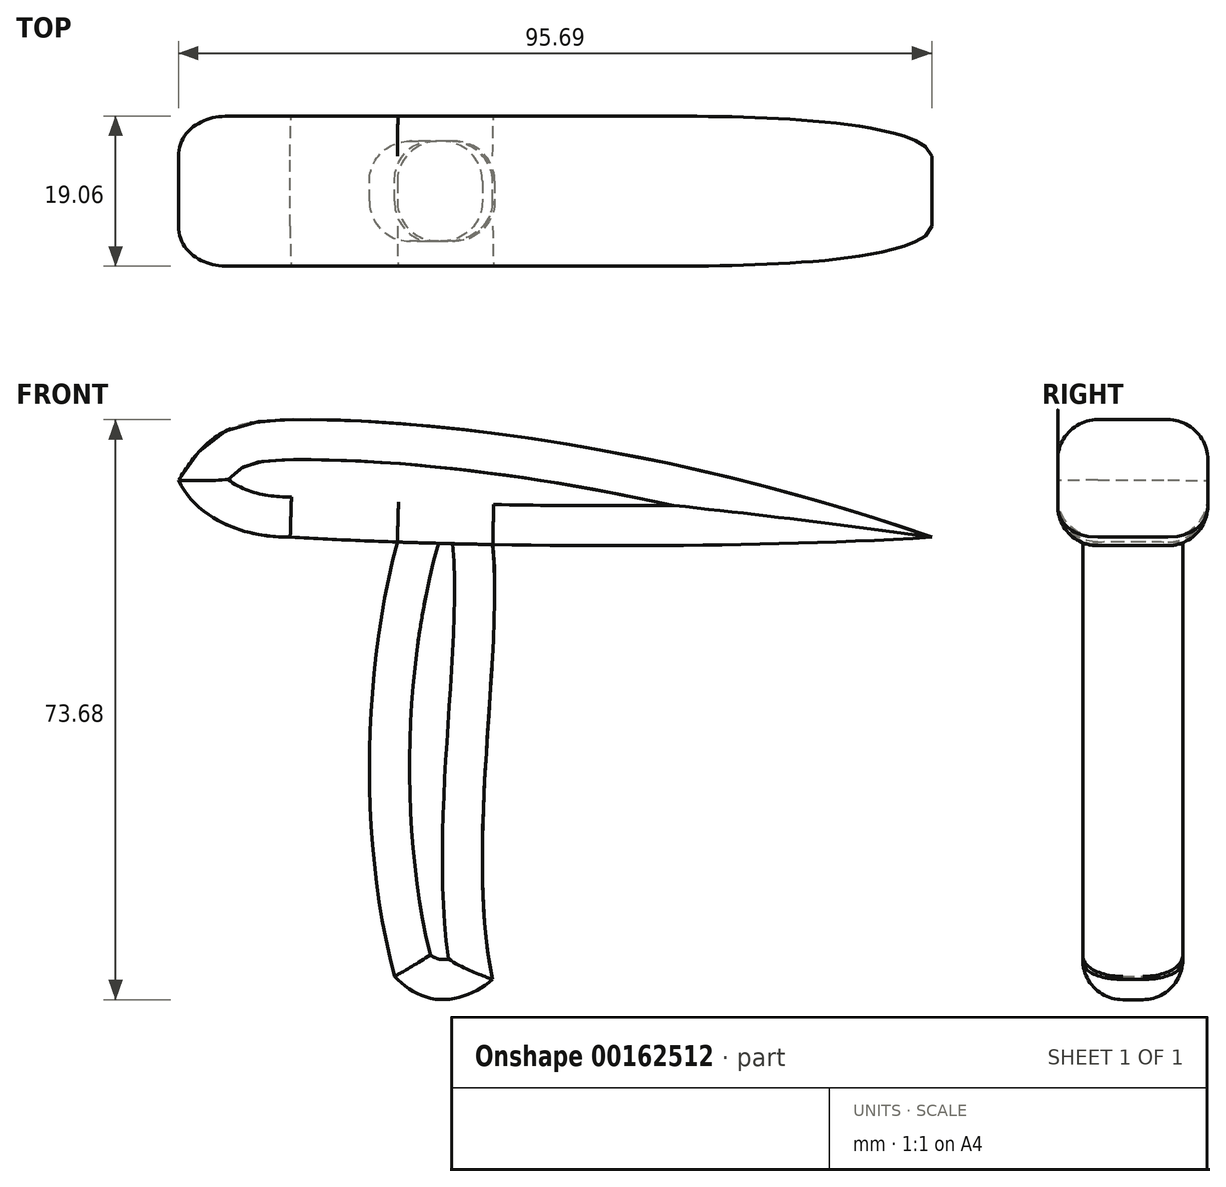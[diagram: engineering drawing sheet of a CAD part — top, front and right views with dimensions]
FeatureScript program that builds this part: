
annotation { "Feature Type Name" : "Feature", "Feature Type Description" : "" }
export const myFeature = defineFeature(function(context is Context, id is Id, definition is map)
    precondition{}
    {
        {
            var Q0;
            Q0=qCreatedBy(makeId("Front.planeOp"),FACE);
            var sketch = newSketch(context, id + "F0", { "sketchPlane" : qUnion([Q0])});
            skFitSpline(sketch, "E0", {"points": [v(-18.74, 0) * mm, v(-32.94, 7.24) * mm], "startDerivative": vector(-21.3, 0) * mm, "endDerivative": vector(-5.96, 12.78) * mm});
            skFitSpline(sketch, "E1", {"points": [v(-32.94, 7.24) * mm, v(-18.74, 14.9) * mm, v(62.75, 0) * mm], "startDerivative": vector(40.42, 66.4) * mm, "endDerivative": vector(151.04, -52.56) * mm});
            skFitSpline(sketch, "E2", {"points": [v(-18.74, 0) * mm, v(62.75, 0) * mm], "startDerivative": vector(64.51, -3.85) * mm, "endDerivative": vector(77.53, 4.86) * mm});
            skFitSpline(sketch, "E3", {"points": [v(-5.14, -0.63) * mm, v(-5.5, -55.81) * mm], "startDerivative": vector(-13.18, -49.42) * mm, "endDerivative": vector(13.65, -52) * mm});
            skFitSpline(sketch, "E4", {"points": [v(6.99, -0.94) * mm, v(6.97, -56.18) * mm], "startDerivative": vector(4.1, -40.3) * mm, "endDerivative": vector(10.6, -49.2) * mm});
            skFitSpline(sketch, "E5", {"points": [v(-5.5, -55.81) * mm, v(6.97, -56.18) * mm], "startDerivative": vector(11.23, -11.78) * mm, "endDerivative": vector(12.55, 10.29) * mm});
            skLineSegment(sketch, "E6", {"start": v(-5.14, -0.63) * mm, "end": v(6.99, -0.94) * mm});
            skSolve(sketch);
        }
        {
            var Q0;
            {var subQ3=sQuery(id+"F0.wireOp",EDGE,"E0");Q0=makeQuery(id+"F0.imprint","IMPRINT",FACE,{"disambiguationData":[TD([[makeQuery(id+"F0.imprint","IMPRINT",EDGE,{"derivedFrom":subQ3}),-1.0]])]});}
            var Q1;
            {var subQ1=sQuery(id+"F0.wireOp",EDGE,"E3");Q1=makeQuery(id+"F0.imprint","IMPRINT",FACE,{"disambiguationData":[TD([[makeQuery(id+"F0.imprint","IMPRINT",EDGE,{"derivedFrom":subQ1}),1.0]])]});}
            extrude(context, id + "F1", {"entities" : qUnion([Q0, Q1]), "endBound" : BoundingType.SYMMETRIC, "depth" : 12.7 * mm});
        }
        {
            var Q0;
            Q0=makeQuery(id+"F1.opExtrude","CAP_FACE",FACE,{"disambiguationData":[OSD([sQuery(id+"F0.wireOp",EDGE,"E0"),sQuery(id+"F0.wireOp",EDGE,"E1"),sQuery(id+"F0.wireOp",EDGE,"E2"),sQuery(id+"F0.wireOp",EDGE,"E6")])],"isStart":false});
            var Q1;
            Q1=makeQuery(id+"F1.opExtrude","CAP_FACE",FACE,{"disambiguationData":[OSD([sQuery(id+"F0.wireOp",EDGE,"E0"),sQuery(id+"F0.wireOp",EDGE,"E1"),sQuery(id+"F0.wireOp",EDGE,"E2"),sQuery(id+"F0.wireOp",EDGE,"E6")])],"isStart":true});
            extrude(context, id + "F2", {"entities" : qUnion([Q0, Q1]), "operationType" : NewBodyOperationType.ADD, "endBound" : BoundingType.SYMMETRIC, "depth" : 6.35 * mm});
        }
        {
            var Q0;
            {var subQ0=sQuery(id+"F0.wireOp",EDGE,"E1");Q0=makeQuery(id+"F2.opExtrude","CAP_EDGE",EDGE,{"disambiguationData":[OSD([subQ0]),TDD([makeQuery(id+"F1.opExtrude","CAP_EDGE",EDGE,{"disambiguationData":[OSD([subQ0])],"isStart":false})])],"isStart":false});}
            var Q1;
            {var subQ0=sQuery(id+"F0.wireOp",EDGE,"E6");var subQ1=sQuery(id+"F0.wireOp",EDGE,"E2");var subQ2=sQuery(id+"F0.wireOp",EDGE,"E1");var subQ3=sQuery(id+"F0.wireOp",EDGE,"E0");Q1=makeQuery(id+"F2.opExtrude","CAP_FACE",FACE,{"disambiguationData":[OSD([subQ3,subQ2,subQ1,subQ0]),TDD([makeQuery(id+"F1.opExtrude","CAP_FACE",FACE,{"disambiguationData":[OSD([subQ3,subQ2,subQ1,subQ0])],"isStart":false})])],"isStart":false});}
            var Q2;
            {var subQ0=sQuery(id+"F0.wireOp",EDGE,"E1");Q2=makeQuery(id+"F2.opExtrude","CAP_EDGE",EDGE,{"disambiguationData":[OSD([subQ0]),TDD([makeQuery(id+"F1.opExtrude","CAP_EDGE",EDGE,{"disambiguationData":[OSD([subQ0])],"isStart":true})])],"isStart":true});}
            var Q3;
            {var subQ0=sQuery(id+"F0.wireOp",EDGE,"E0");Q3=makeQuery(id+"F2.opExtrude","CAP_EDGE",EDGE,{"disambiguationData":[OSD([subQ0]),TDD([makeQuery(id+"F1.opExtrude","CAP_EDGE",EDGE,{"disambiguationData":[OSD([subQ0])],"isStart":true})])],"isStart":true});}
            var Q4;
            Q4=makeQuery(id+"F1.opExtrude","CAP_EDGE",EDGE,{"disambiguationData":[OSD([sQuery(id+"F0.wireOp",EDGE,"E3")])],"isStart":false});
            var Q5;
            Q5=makeQuery(id+"F1.opExtrude","CAP_EDGE",EDGE,{"disambiguationData":[OSD([sQuery(id+"F0.wireOp",EDGE,"E3")])],"isStart":true});
            var Q6;
            Q6=makeQuery(id+"F1.opExtrude","CAP_EDGE",EDGE,{"disambiguationData":[OSD([sQuery(id+"F0.wireOp",EDGE,"E4")])],"isStart":false});
            var Q7;
            Q7=makeQuery(id+"F1.opExtrude","CAP_EDGE",EDGE,{"disambiguationData":[OSD([sQuery(id+"F0.wireOp",EDGE,"E5")])],"isStart":false});
            var Q8;
            Q8=makeQuery(id+"F1.opExtrude","CAP_EDGE",EDGE,{"disambiguationData":[OSD([sQuery(id+"F0.wireOp",EDGE,"E5")])],"isStart":true});
            var Q9;
            Q9=makeQuery(id+"F1.opExtrude","CAP_EDGE",EDGE,{"disambiguationData":[OSD([sQuery(id+"F0.wireOp",EDGE,"E4")])],"isStart":true});
            fillet(context, id + "F3", {"entities" : qUnion([Q0, Q1, Q2, Q3, Q4, Q5, Q6, Q7, Q8, Q9]), "radius" : 5.08 * mm, "tangentPropagation" : true, "allowEdgeOverflow" : false});
        }
    });
